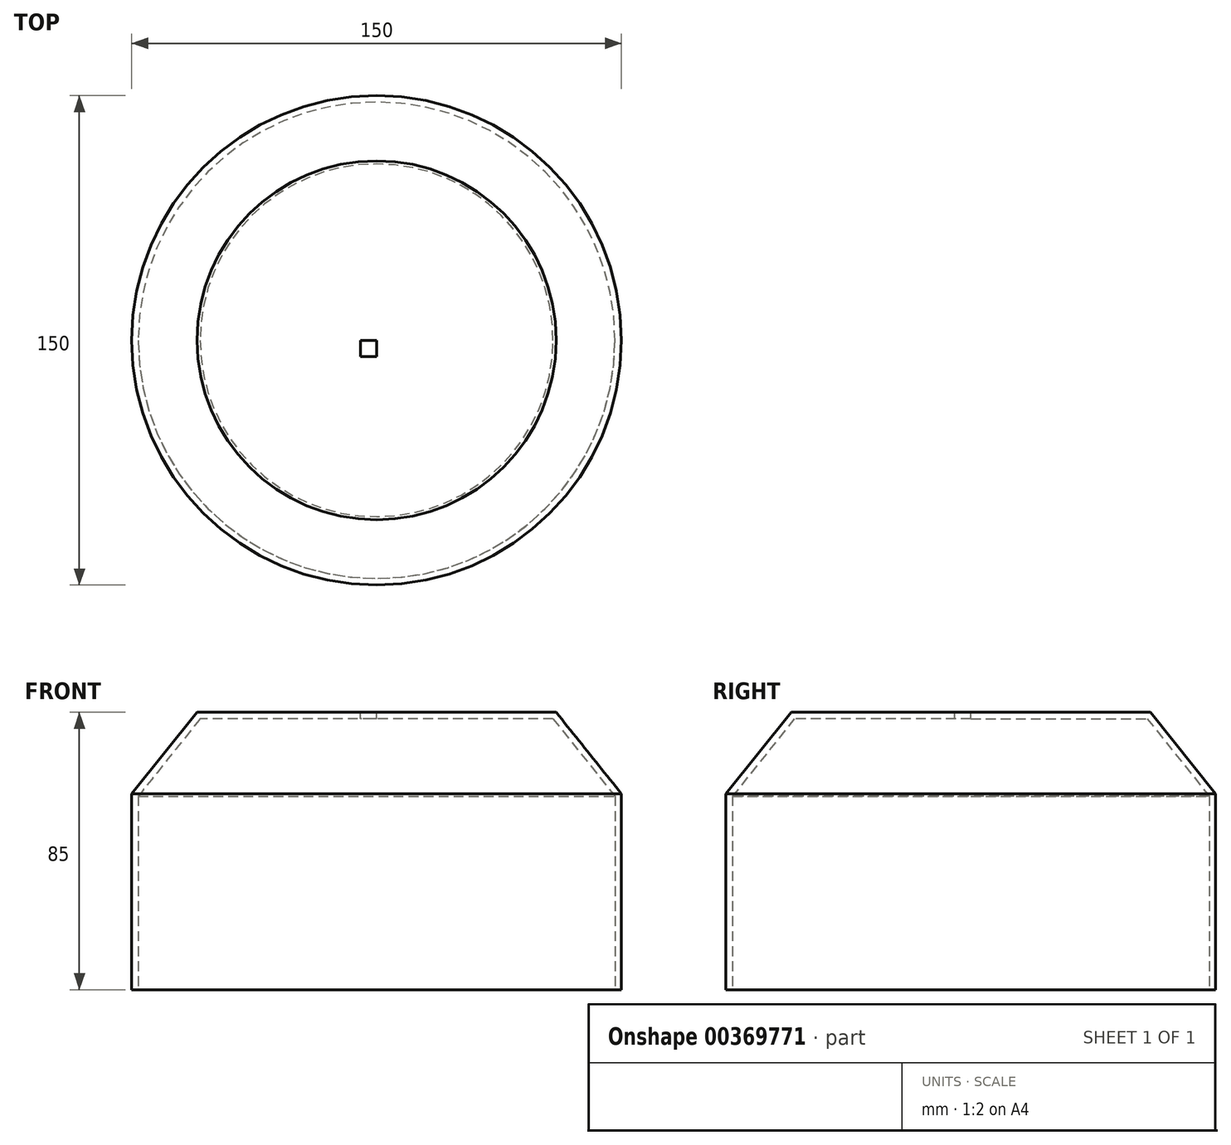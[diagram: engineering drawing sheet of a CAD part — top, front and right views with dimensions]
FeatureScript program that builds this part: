
annotation { "Feature Type Name" : "Feature", "Feature Type Description" : "" }
export const myFeature = defineFeature(function(context is Context, id is Id, definition is map)
    precondition{}
    {
        {
            var Q0;
            Q0=qCreatedBy(makeId("Top.planeOp"),FACE);
            var sketch = newSketch(context, id + "F0", { "sketchPlane" : qUnion([Q0])});
            skCircle(sketch, "E0", {"center": v(0, 0) * mm, "radius": 75 * mm});
            skSolve(sketch);
        }
        {
            var Q0;
            Q0 = qSketchRegion(id + "F0", true);
            var Q1;
            Q1=sQuery(id+"F0.wireOp",EDGE,"E0");
            extrude(context, id + "F1", {"entities" : qUnion([Q0]), "surfaceEntities" : qUnion([Q1]), "depth" : 85 * mm, "offsetDistance" : 25 * mm});
        }
        {
            var Q0;
            Q0=makeQuery(id+"F1.opExtrude","CAP_EDGE",EDGE,{"disambiguationData":[OSD([sQuery(id+"F0.wireOp",EDGE,"E0")])],"isStart":false});
            chamfer(context, id + "F2", {"entities" : qUnion([Q0]), "chamferType" : ChamferType.TWO_OFFSETS, "width1" : 20 * mm, "oppositeDirection" : false, "width2" : 25 * mm, "tangentPropagation" : true});
        }
        {
            var Q0;
            Q0=makeQuery(id+"F1.opExtrude","CAP_FACE",FACE,{"disambiguationData":[OSD([sQuery(id+"F0.wireOp",EDGE,"E0")])],"isStart":true});
            shell(context, id + "F3", {"entities" : qUnion([Q0]), "thickness" : 2 * mm});
        }
        {
            var Q0;
            Q0=makeQuery(id+"F1.opExtrude","CAP_FACE",FACE,{"disambiguationData":[OSD([sQuery(id+"F0.wireOp",EDGE,"E0")])],"isStart":false});
            var sketch = newSketch(context, id + "F4", { "sketchPlane" : qUnion([Q0])});
            skLineSegment(sketch, "E1.bottom", {"start": v(0, 0) * mm, "end": v(-5, 0) * mm});
            skLineSegment(sketch, "E1.top", {"start": v(0, -5) * mm, "end": v(-5, -5) * mm});
            skLineSegment(sketch, "E1.left", {"start": v(0, 0) * mm, "end": v(0, -5) * mm});
            skLineSegment(sketch, "E1.right", {"start": v(-5, 0) * mm, "end": v(-5, -5) * mm});
            skLineSegment(sketch, "E2", {"start": v(0, -79.53) * mm, "end": v(0, 101.94) * mm, "construction": true});
            skSolve(sketch);
        }
        {
            var Q0;
            {var subQ0=sQuery(id+"F4.wireOp",EDGE,"E1.bottom");Q0=makeQuery(id+"F4.imprint","IMPRINT",FACE,{"disambiguationData":[TD([[makeQuery(id+"F4.imprint","IMPRINT",EDGE,{"derivedFrom":subQ0}),1.0]])]});}
            extrude(context, id + "F5", {"entities" : qUnion([Q0]), "operationType" : NewBodyOperationType.REMOVE, "endBound" : BoundingType.THROUGH_ALL, "oppositeDirection" : true, "depth" : 25 * mm, "offsetDistance" : 25 * mm});
        }
        {
            var Q0;
            Q0=qCreatedBy(makeId("Top.planeOp"),FACE);
            var sketch = newSketch(context, id + "F6", { "sketchPlane" : qUnion([Q0])});
            skCircle(sketch, "E3", {"center": v(0, 0) * mm, "radius": 65 * mm});
            skSolve(sketch);
        }
        {
            var Q0;
            Q0=makeQuery(id+"F6.imprint","IMPRINT",FACE,{"disambiguationData":[TD([[makeQuery(id+"F6.imprint","IMPRINT",EDGE,{"derivedFrom":sQuery(id+"F6.wireOp",EDGE,"E3")}),1.0]])]});
            var Q1;
            Q1 = qConstructionFilter(qBodyType(qCreatedBy(id + "F6" ,EDGE), BodyType.WIRE), ConstructionObject.NO);
            extrude(context, id + "F7", {"entities" : qUnion([Q0]), "bodyType" : ToolBodyType.SURFACE, "operationType" : NewBodyOperationType.ADD, "surfaceEntities" : qUnion([Q1]), "endBound" : BoundingType.UP_TO_NEXT, "depth" : 60 * mm, "hasOffset" : true, "offsetDistance" : 25 * mm});
        }
    });
